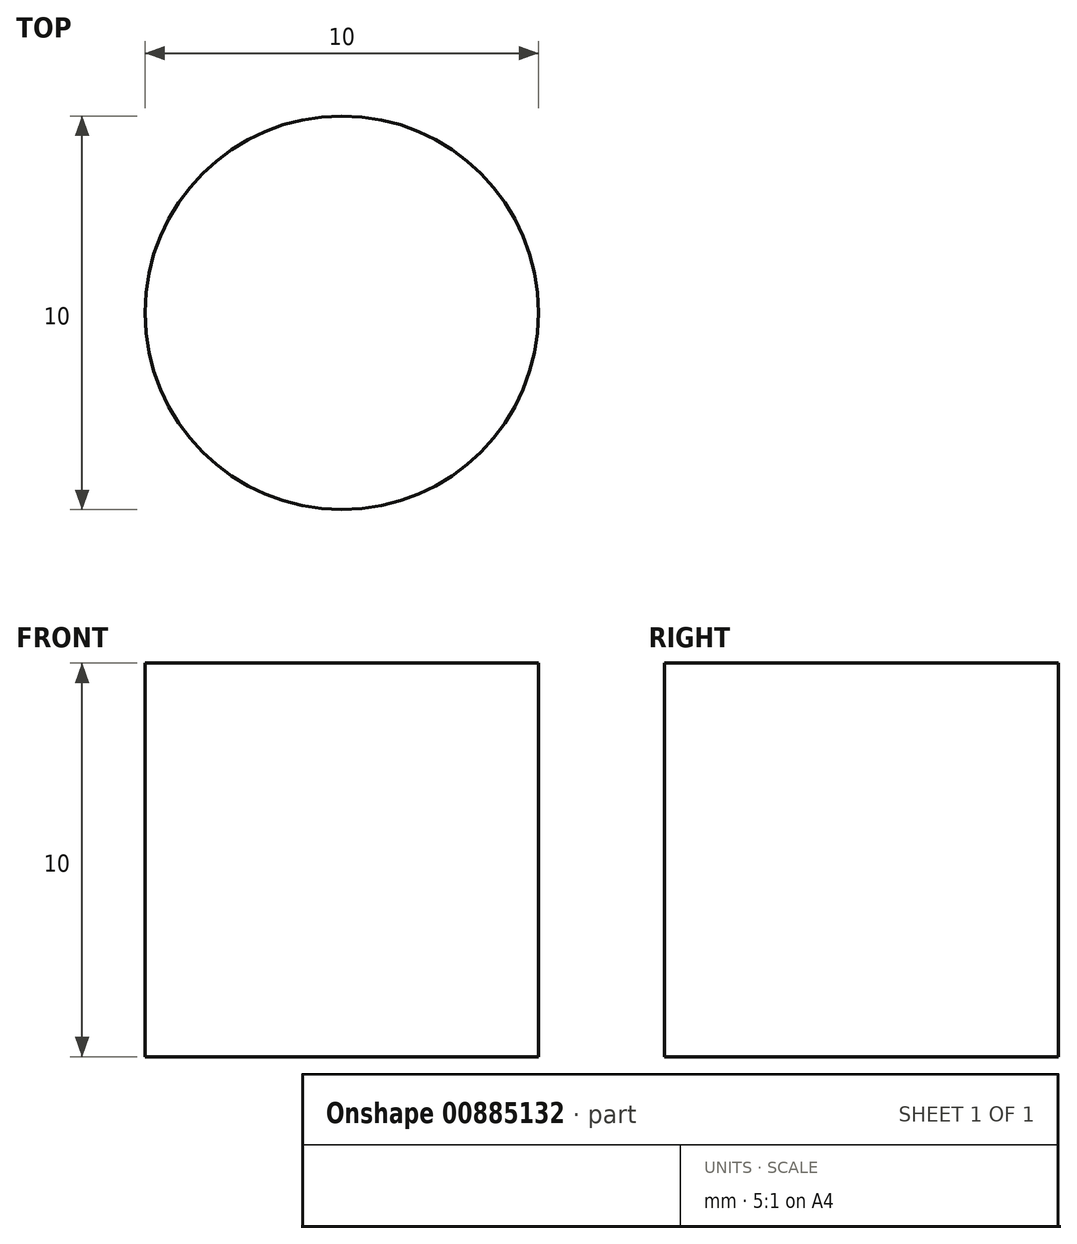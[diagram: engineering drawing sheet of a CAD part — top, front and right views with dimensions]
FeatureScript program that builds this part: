
annotation { "Feature Type Name" : "Feature", "Feature Type Description" : "" }
export const myFeature = defineFeature(function(context is Context, id is Id, definition is map)
    precondition{}
    {
        {
            var Q0;
            Q0=qCreatedBy(makeId("Top.planeOp"),FACE);
            var sketch = newSketch(context, id + "F0", { "sketchPlane" : qUnion([Q0])});
            skCircle(sketch, "E0", {"center": v(0, 0) * mm, "radius": 5 * mm});
            skSolve(sketch);
        }
        {
            var Q0;
            Q0 = qSketchRegion(id + "F0", true);
            extrude(context, id + "F1", {"entities" : qUnion([Q0]), "depth" : 10 * mm, "offsetDistance" : 25 * mm});
        }
    });
